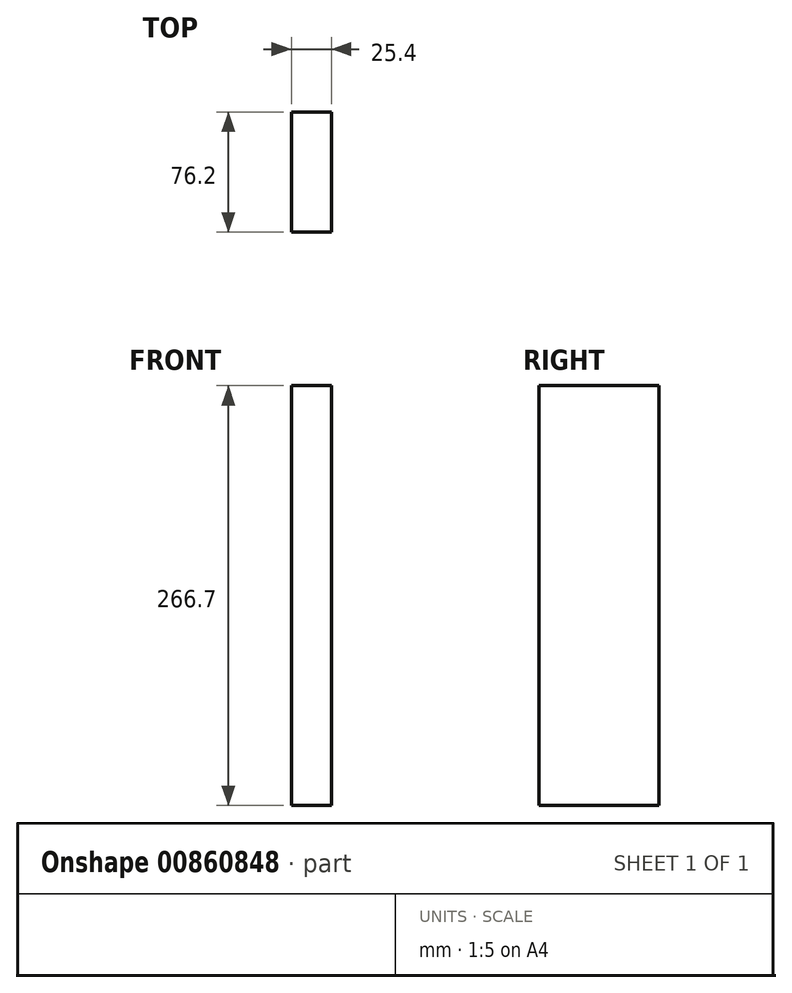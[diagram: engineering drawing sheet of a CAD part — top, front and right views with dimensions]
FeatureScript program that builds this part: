
annotation { "Feature Type Name" : "Feature", "Feature Type Description" : "" }
export const myFeature = defineFeature(function(context is Context, id is Id, definition is map)
    precondition{}
    {
        {
            var Q0;
            Q0=qCreatedBy(makeId("Front.planeOp"),FACE);
            var sketch = newSketch(context, id + "F0", { "sketchPlane" : qUnion([Q0])});
            skLineSegment(sketch, "E0.bottom", {"start": v(-91.4, 148.44) * mm, "end": v(-66, 148.44) * mm});
            skLineSegment(sketch, "E0.top", {"start": v(-91.4, -118.26) * mm, "end": v(-66, -118.26) * mm});
            skLineSegment(sketch, "E0.left", {"start": v(-91.4, 148.44) * mm, "end": v(-91.4, -118.26) * mm});
            skLineSegment(sketch, "E0.right", {"start": v(-66, 148.44) * mm, "end": v(-66, -118.26) * mm});
            skSolve(sketch);
        }
        {
            var Q0;
            Q0 = qSketchRegion(id + "F0", true);
            extrude(context, id + "F1", {"entities" : qUnion([Q0]), "depth" : 76.2 * mm, "offsetDistance" : 25.4 * mm});
        }
    });
